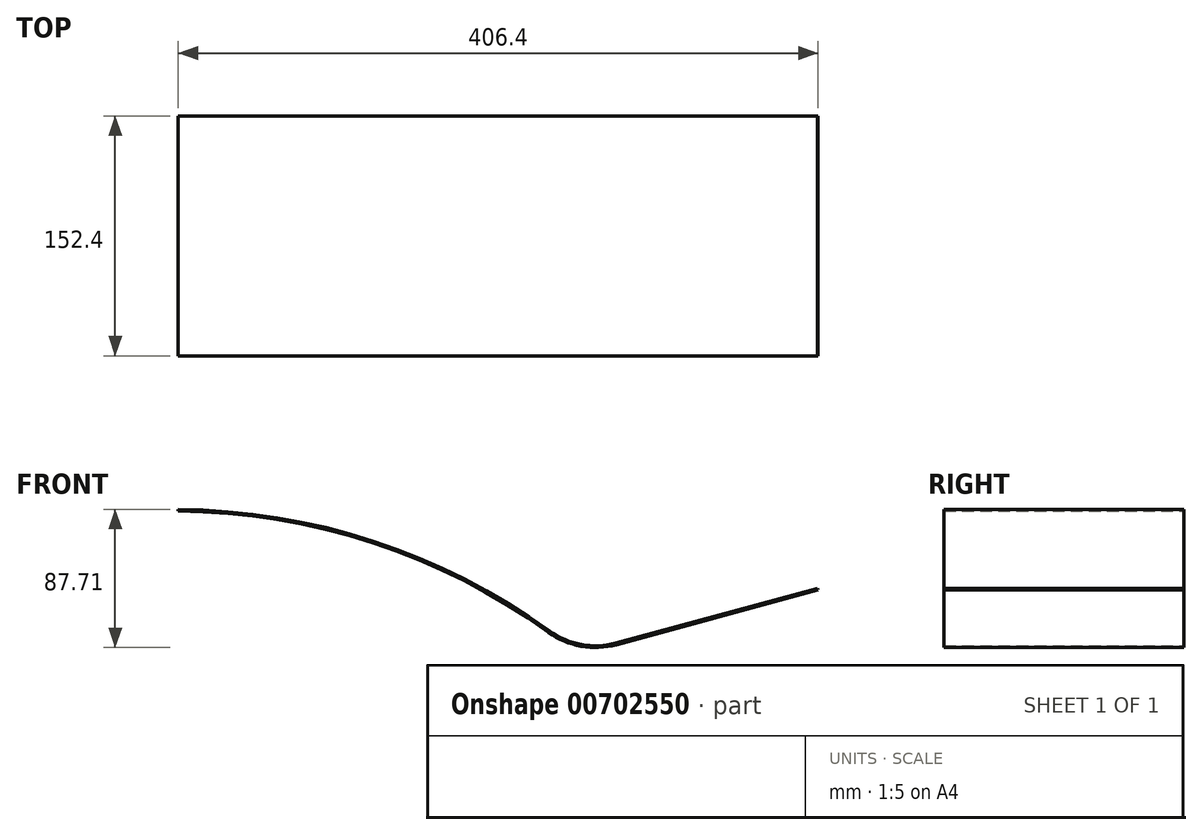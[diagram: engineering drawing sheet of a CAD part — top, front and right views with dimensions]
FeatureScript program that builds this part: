
annotation { "Feature Type Name" : "Feature", "Feature Type Description" : "" }
export const myFeature = defineFeature(function(context is Context, id is Id, definition is map)
    precondition{}
    {
        {
            var Q0;
            Q0=qCreatedBy(makeId("Front.planeOp"),FACE);
            var sketch = newSketch(context, id + "F0", { "sketchPlane" : qUnion([Q0])});
            skArc(sketch, "E0", {"start": v(-18.79, 14.43) * mm, "mid": v(-130.39, 71.28) * mm, "end": v(-254, 91.44) * mm});
            skLineSegment(sketch, "E1", {"start": v(24.25, 6.57) * mm, "end": v(152.4, 41.27) * mm});
            skLineSegment(sketch, "E2", {"start": v(-254, 0) * mm, "end": v(152.4, 0) * mm, "construction": true});
            skLineSegment(sketch, "E3", {"start": v(-254, 0) * mm, "end": v(-254, 91.44) * mm, "construction": true});
            skLineSegment(sketch, "E4", {"start": v(152.4, 41.27) * mm, "end": v(152.4, 0) * mm, "construction": true});
            skPoint(sketch, "E5.visualSharp", {"position": v(0, 0) * mm});
            skArc(sketch, "E5.filletArc", {"start": v(-18.79, 14.43) * mm, "mid": v(1.84, 5.63) * mm, "end": v(24.25, 6.57) * mm});
            skArc(sketch, "E6.0", {"start": v(-18.16, 15.3) * mm, "mid": v(-130.06, 72.29) * mm, "end": v(-254, 92.5) * mm});
            skArc(sketch, "E6.1", {"start": v(-18.16, 15.3) * mm, "mid": v(2.03, 6.68) * mm, "end": v(23.97, 7.6) * mm});
            skLineSegment(sketch, "E6.2", {"start": v(23.97, 7.6) * mm, "end": v(152.12, 42.3) * mm});
            skLineSegment(sketch, "E7", {"start": v(152.12, 42.3) * mm, "end": v(152.4, 41.27) * mm});
            skLineSegment(sketch, "E8", {"start": v(-254, 92.5) * mm, "end": v(-254, 91.44) * mm});
            skSolve(sketch);
        }
        {
            var Q0;
            Q0 = qSketchRegion(id + "F0", true);
            extrude(context, id + "F1", {"entities" : qUnion([Q0]), "depth" : 76.2 * mm, "offsetDistance" : 25.4 * mm, "hasSecondDirection" : true, "secondDirectionOppositeDirection" : true, "secondDirectionDepth" : 76.2 * mm});
        }
    });
